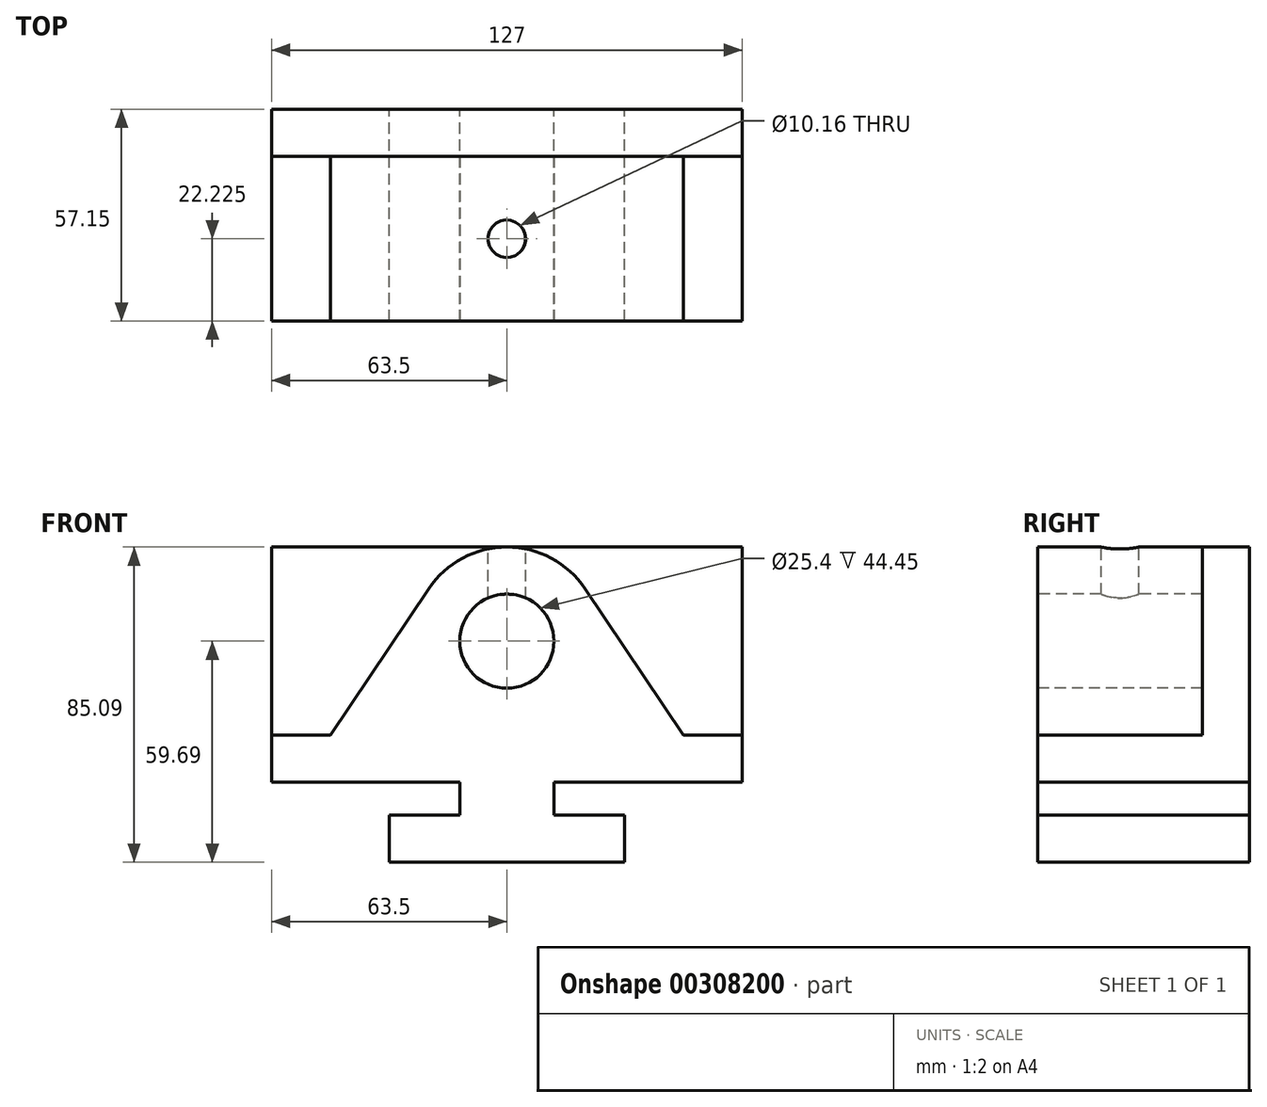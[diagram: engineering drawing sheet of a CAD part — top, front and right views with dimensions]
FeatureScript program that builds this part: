
annotation { "Feature Type Name" : "Feature", "Feature Type Description" : "" }
export const myFeature = defineFeature(function(context is Context, id is Id, definition is map)
    precondition{}
    {
        {
            var Q0;
            Q0=qCreatedBy(makeId("Front.planeOp"),FACE);
            var sketch = newSketch(context, id + "F0", { "sketchPlane" : qUnion([Q0])});
            skLineSegment(sketch, "E0", {"start": v(0, 0) * mm, "end": v(0, 63.5) * mm});
            skLineSegment(sketch, "E1", {"start": v(0, 63.5) * mm, "end": v(127, 63.5) * mm});
            skLineSegment(sketch, "E2", {"start": v(127, 63.5) * mm, "end": v(127, 0) * mm});
            skLineSegment(sketch, "E3", {"start": v(127, 0) * mm, "end": v(76.2, 0) * mm});
            skLineSegment(sketch, "E4", {"start": v(76.2, 0) * mm, "end": v(76.2, -8.89) * mm});
            skLineSegment(sketch, "E5", {"start": v(76.2, -8.9) * mm, "end": v(95.25, -8.9) * mm});
            skLineSegment(sketch, "E6", {"start": v(95.25, -8.89) * mm, "end": v(95.25, -21.59) * mm});
            skLineSegment(sketch, "E7", {"start": v(95.25, -21.59) * mm, "end": v(31.75, -21.59) * mm});
            skLineSegment(sketch, "E8", {"start": v(31.75, -21.59) * mm, "end": v(31.75, -8.9) * mm});
            skLineSegment(sketch, "E9", {"start": v(31.75, -8.9) * mm, "end": v(50.8, -8.89) * mm});
            skLineSegment(sketch, "E10", {"start": v(50.8, -8.89) * mm, "end": v(50.8, 0) * mm});
            skLineSegment(sketch, "E11", {"start": v(50.8, 0) * mm, "end": v(0, 0) * mm});
            skLineSegment(sketch, "E12", {"start": v(63.5, 63.5) * mm, "end": v(63.5, -21.59) * mm, "construction": true});
            skPoint(sketch, "E13.orphan", {"position": v(63.5, 0) * mm});
            skSolve(sketch);
        }
        {
            var Q0;
            Q0 = qSketchRegion(id + "F0", true);
            extrude(context, id + "F1", {"entities" : qUnion([Q0]), "depth" : 57.15 * mm});
        }
        {
            var Q0;
            Q0=makeQuery(id+"F1.opExtrude","CAP_FACE",FACE,{"disambiguationData":[OSD([sQuery(id+"F0.wireOp",EDGE,"E0"),sQuery(id+"F0.wireOp",EDGE,"E1"),sQuery(id+"F0.wireOp",EDGE,"E2"),sQuery(id+"F0.wireOp",EDGE,"E3"),sQuery(id+"F0.wireOp",EDGE,"E4"),sQuery(id+"F0.wireOp",EDGE,"E5"),sQuery(id+"F0.wireOp",EDGE,"E6"),sQuery(id+"F0.wireOp",EDGE,"E7"),sQuery(id+"F0.wireOp",EDGE,"E8"),sQuery(id+"F0.wireOp",EDGE,"E9"),sQuery(id+"F0.wireOp",EDGE,"E10"),sQuery(id+"F0.wireOp",EDGE,"E11")])],"isStart":false});
            var sketch = newSketch(context, id + "F2", { "sketchPlane" : qUnion([Q0])});
            skLineSegment(sketch, "E14", {"start": v(63.5, 63.5) * mm, "end": v(63.5, -21.59) * mm, "construction": true});
            skLineSegment(sketch, "E15", {"start": v(0, 12.7) * mm, "end": v(15.87, 12.7) * mm});
            skLineSegment(sketch, "E16", {"start": v(15.87, 12.7) * mm, "end": v(42.4, 52.25) * mm});
            skLineSegment(sketch, "E17", {"start": v(127, 12.7) * mm, "end": v(111.13, 12.7) * mm});
            skLineSegment(sketch, "E18", {"start": v(111.12, 12.7) * mm, "end": v(84.6, 52.25) * mm});
            skArc(sketch, "E19", {"start": v(84.6, 52.25) * mm, "mid": v(63.5, 63.5) * mm, "end": v(42.4, 52.25) * mm});
            skCircle(sketch, "E20", {"center": v(63.5, 38.1) * mm, "radius": 12.7 * mm});
            skSolve(sketch);
        }
        {
            var Q0;
            Q0 = qSketchRegion(id + "F2", true);
            extrude(context, id + "F3", {"entities" : qUnion([Q0]), "operationType" : NewBodyOperationType.REMOVE, "oppositeDirection" : true, "depth" : 44.45 * mm});
        }
        {
            var Q0;
            {var subQ3=sQuery(id+"F2.wireOp",EDGE,"E15");Q0=makeQuery(id+"F2.imprint","IMPRINT",FACE,{"disambiguationData":[TD([[makeQuery(id+"F2.imprint","IMPRINT",EDGE,{"derivedFrom":subQ3}),1.0]])]});}
            var Q1;
            {var subQ6=sQuery(id+"F2.wireOp",EDGE,"E17");Q1=makeQuery(id+"F2.imprint","IMPRINT",FACE,{"disambiguationData":[TD([[makeQuery(id+"F2.imprint","IMPRINT",EDGE,{"derivedFrom":subQ6}),-1.0]])]});}
            extrude(context, id + "F4", {"entities" : qUnion([Q0, Q1]), "operationType" : NewBodyOperationType.REMOVE, "oppositeDirection" : true, "depth" : 44.45 * mm});
        }
        {
            var Q0;
            Q0=makeQuery(id+"F1.opExtrude","SWEPT_FACE",FACE,{"disambiguationData":[OSD([sQuery(id+"F0.wireOp",EDGE,"E1")])]});
            var sketch = newSketch(context, id + "F5", { "sketchPlane" : qUnion([Q0])});
            skLineSegment(sketch, "E21.bottom", {"start": v(0, 0) * mm, "end": v(126.8, 0) * mm});
            skLineSegment(sketch, "E21.top", {"start": v(0, -57.15) * mm, "end": v(126.8, -57.15) * mm});
            skLineSegment(sketch, "E21.left", {"start": v(0, 0) * mm, "end": v(0, -57.15) * mm});
            skLineSegment(sketch, "E21.right", {"start": v(126.8, 0) * mm, "end": v(126.8, -57.15) * mm});
            skLineSegment(sketch, "E22", {"start": v(63.5, -12.7) * mm, "end": v(63.5, -57.15) * mm, "construction": true});
            skCircle(sketch, "E23", {"center": v(63.5, -34.93) * mm, "radius": 5.08 * mm});
            skSolve(sketch);
        }
        {
            var Q0;
            Q0=makeQuery(id+"F5.imprint","IMPRINT",FACE,{"disambiguationData":[TD([[makeQuery(id+"F5.imprint","IMPRINT",EDGE,{"derivedFrom":sQuery(id+"F5.wireOp",EDGE,"E23")}),1.0]])]});
            extrude(context, id + "F6", {"entities" : qUnion([Q0]), "operationType" : NewBodyOperationType.REMOVE, "oppositeDirection" : true, "depth" : 25.4 * mm});
        }
    });
